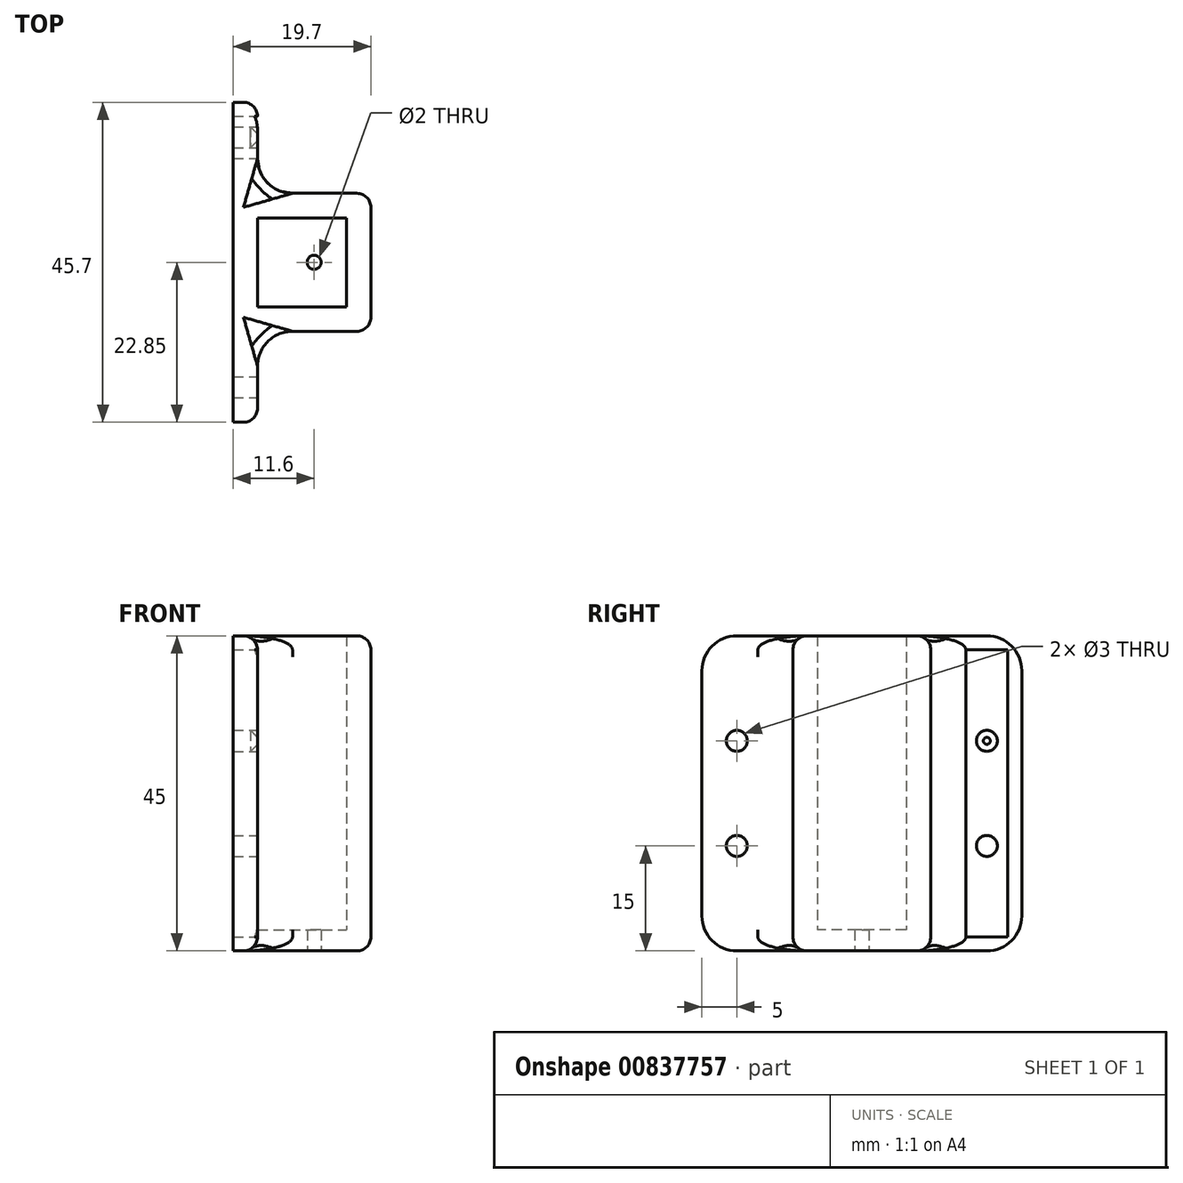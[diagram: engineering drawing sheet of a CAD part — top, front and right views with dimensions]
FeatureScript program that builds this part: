
annotation { "Feature Type Name" : "Feature", "Feature Type Description" : "" }
export const myFeature = defineFeature(function(context is Context, id is Id, definition is map)
    precondition{}
    {
        {
            var Q0;
            Q0=qCreatedBy(makeId("Top.planeOp"),FACE);
            var sketch = newSketch(context, id + "F0", { "sketchPlane" : qUnion([Q0])});
            skLineSegment(sketch, "E0.bottom", {"start": v(0, 6.35) * mm, "end": v(12.7, 6.35) * mm});
            skLineSegment(sketch, "E0.top", {"start": v(0, -6.35) * mm, "end": v(12.7, -6.35) * mm});
            skLineSegment(sketch, "E0.left", {"start": v(0, 6.35) * mm, "end": v(0, -6.35) * mm});
            skLineSegment(sketch, "E0.right", {"start": v(12.7, 6.35) * mm, "end": v(12.7, -6.35) * mm});
            skLineSegment(sketch, "E1.0", {"start": v(0, 9.85) * mm, "end": v(16.2, 9.85) * mm});
            skLineSegment(sketch, "E1.1", {"start": v(-3.5, 9.85) * mm, "end": v(-3.5, -9.85) * mm});
            skLineSegment(sketch, "E1.2", {"start": v(0, -9.85) * mm, "end": v(16.2, -9.85) * mm});
            skLineSegment(sketch, "E1.3", {"start": v(16.2, 9.85) * mm, "end": v(16.2, -9.85) * mm});
            skLineSegment(sketch, "E2.top", {"start": v(-3.5, 22.85) * mm, "end": v(0, 22.85) * mm});
            skLineSegment(sketch, "E2.left", {"start": v(-3.5, -9.85) * mm, "end": v(-3.5, 22.85) * mm});
            skLineSegment(sketch, "E3.trimOffspring", {"start": v(0, -6.35) * mm, "end": v(0, 6.35) * mm});
            skPoint(sketch, "E2.bottom.start.orphan", {"position": v(-3.5, -21.69) * mm});
            skLineSegment(sketch, "E4.trimOffspring", {"start": v(0, 9.85) * mm, "end": v(0, 22.85) * mm});
            skLineSegment(sketch, "E5.MirrorCS", {"start": v(0, -9.85) * mm, "end": v(0, -22.85) * mm});
            skLineSegment(sketch, "E6.MirrorCS", {"start": v(-3.5, -22.85) * mm, "end": v(0, -22.85) * mm});
            skLineSegment(sketch, "E7.MirrorCS", {"start": v(-3.5, 9.85) * mm, "end": v(-3.5, -22.85) * mm});
            skSolve(sketch);
        }
        {
            var Q0;
            Q0 = qSketchRegion(id + "F0", true);
            extrude(context, id + "F1", {"entities" : qUnion([Q0]), "depth" : 45 * mm, "offsetDistance" : 25 * mm});
        }
        {
            var Q0;
            Q0=makeQuery(id+"F0.imprint","IMPRINT",FACE,{"disambiguationData":[TD([[makeQuery(id+"F0.imprint","IMPRINT",EDGE,{"derivedFrom":sQuery(id+"F0.wireOp",EDGE,"E0.bottom")}),-1.0]])]});
            extrude(context, id + "F2", {"entities" : qUnion([Q0]), "operationType" : NewBodyOperationType.ADD, "depth" : 3 * mm, "offsetDistance" : 25 * mm});
        }
        {
            var Q0;
            {var subQ0=sQuery(id+"F0.wireOp",EDGE,"E3.trimOffspring");var subQ1=sQuery(id+"F0.wireOp",EDGE,"E0.right");var subQ2=sQuery(id+"F0.wireOp",EDGE,"E0.top");var subQ3=sQuery(id+"F0.wireOp",EDGE,"E0.bottom");Q0=makeQuery(id+"F2.boolean.opBoolean","MERGE",FACE,{"derivedFrom":[makeQuery(id+"F1.opExtrude","CAP_FACE",FACE,{"disambiguationData":[OSD([subQ3,subQ2,subQ1,sQuery(id+"F0.wireOp",EDGE,"E1.0"),sQuery(id+"F0.wireOp",EDGE,"E1.2"),sQuery(id+"F0.wireOp",EDGE,"E1.3"),sQuery(id+"F0.wireOp",EDGE,"E2.top"),sQuery(id+"F0.wireOp",EDGE,"E2.left"),subQ0,sQuery(id+"F0.wireOp",EDGE,"E4.trimOffspring"),sQuery(id+"F0.wireOp",EDGE,"E5.MirrorCS"),sQuery(id+"F0.wireOp",EDGE,"E6.MirrorCS"),sQuery(id+"F0.wireOp",EDGE,"E7.MirrorCS")])],"isStart":true}),makeQuery(id+"F2.opExtrude","CAP_FACE",FACE,{"disambiguationData":[OSD([subQ3,subQ2,subQ1,subQ0])],"isStart":true})]});}
            var sketch = newSketch(context, id + "F3", { "sketchPlane" : qUnion([Q0])});
            skLineSegment(sketch, "E8", {"start": v(0, 0) * mm, "end": v(16.2, 0) * mm, "construction": true});
            skCircle(sketch, "E9", {"center": v(8.1, 0) * mm, "radius": 1 * mm});
            skSolve(sketch);
        }
        {
            var Q0;
            Q0=makeQuery(id+"F3.imprint","IMPRINT",FACE,{"disambiguationData":[TD([[makeQuery(id+"F3.imprint","IMPRINT",EDGE,{"derivedFrom":sQuery(id+"F3.wireOp",EDGE,"E9")}),1.0]])]});
            extrude(context, id + "F4", {"entities" : qUnion([Q0]), "operationType" : NewBodyOperationType.REMOVE, "endBound" : BoundingType.THROUGH_ALL, "oppositeDirection" : true, "depth" : 25 * mm, "offsetDistance" : 25 * mm});
        }
        {
            var Q0;
            Q0=makeQuery(id+"F1.opExtrude","CAP_EDGE",EDGE,{"disambiguationData":[OSD([sQuery(id+"F0.wireOp",EDGE,"E6.MirrorCS")])],"isStart":false});
            var Q1;
            Q1=makeQuery(id+"F1.opExtrude","CAP_EDGE",EDGE,{"disambiguationData":[OSD([sQuery(id+"F0.wireOp",EDGE,"E2.top")])],"isStart":false});
            var Q2;
            Q2=makeQuery(id+"F1.opExtrude","CAP_EDGE",EDGE,{"disambiguationData":[OSD([sQuery(id+"F0.wireOp",EDGE,"E6.MirrorCS")])],"isStart":true});
            var Q3;
            Q3=makeQuery(id+"F1.opExtrude","CAP_EDGE",EDGE,{"disambiguationData":[OSD([sQuery(id+"F0.wireOp",EDGE,"E2.top")])],"isStart":true});
            fillet(context, id + "F5", {"entities" : qUnion([Q0, Q1, Q2, Q3]), "radius" : 5 * mm, "tangentPropagation" : true, "allowEdgeOverflow" : false});
        }
        {
            var Q0;
            Q0=makeQuery(id+"F1.opExtrude","CAP_EDGE",EDGE,{"disambiguationData":[OSD([sQuery(id+"F0.wireOp",EDGE,"E1.3")])],"isStart":false});
            var Q1;
            Q1=makeQuery(id+"F1.opExtrude","CAP_EDGE",EDGE,{"disambiguationData":[OSD([sQuery(id+"F0.wireOp",EDGE,"E1.2")])],"isStart":false});
            var Q2;
            Q2=makeQuery(id+"F1.opExtrude","CAP_EDGE",EDGE,{"disambiguationData":[OSD([sQuery(id+"F0.wireOp",EDGE,"E1.0")])],"isStart":false});
            var Q3;
            Q3=makeQuery(id+"F1.opExtrude","CAP_EDGE",EDGE,{"disambiguationData":[OSD([sQuery(id+"F0.wireOp",EDGE,"E4.trimOffspring")])],"isStart":false});
            var Q4;
            Q4=makeQuery(id+"F1.opExtrude","CAP_EDGE",EDGE,{"disambiguationData":[OSD([sQuery(id+"F0.wireOp",EDGE,"E5.MirrorCS")])],"isStart":false});
            var Q5;
            Q5=makeQuery(id+"F1.opExtrude","SWEPT_EDGE",EDGE,{"disambiguationData":[OSD([sQuery(id+"F0.wireOp",EDGE,"E5.MirrorCS"),sQuery(id+"F0.wireOp",EDGE,"E6.MirrorCS")])]});
            var Q6;
            Q6=makeQuery(id+"F1.opExtrude","SWEPT_EDGE",EDGE,{"disambiguationData":[OSD([sQuery(id+"F0.wireOp",EDGE,"E2.top"),sQuery(id+"F0.wireOp",EDGE,"E4.trimOffspring")])]});
            var Q7;
            Q7=makeQuery(id+"F1.opExtrude","SWEPT_EDGE",EDGE,{"disambiguationData":[OSD([sQuery(id+"F0.wireOp",EDGE,"E1.2"),sQuery(id+"F0.wireOp",EDGE,"E1.3")])]});
            var Q8;
            Q8=makeQuery(id+"F1.opExtrude","SWEPT_EDGE",EDGE,{"disambiguationData":[OSD([sQuery(id+"F0.wireOp",EDGE,"E1.0"),sQuery(id+"F0.wireOp",EDGE,"E1.3")])]});
            var Q9;
            Q9=makeQuery(id+"F1.opExtrude","CAP_EDGE",EDGE,{"disambiguationData":[OSD([sQuery(id+"F0.wireOp",EDGE,"E1.3")])],"isStart":true});
            var Q10;
            Q10=makeQuery(id+"F1.opExtrude","CAP_EDGE",EDGE,{"disambiguationData":[OSD([sQuery(id+"F0.wireOp",EDGE,"E1.2")])],"isStart":true});
            var Q11;
            Q11=makeQuery(id+"F1.opExtrude","CAP_EDGE",EDGE,{"disambiguationData":[OSD([sQuery(id+"F0.wireOp",EDGE,"E1.0")])],"isStart":true});
            var Q12;
            Q12=makeQuery(id+"F1.opExtrude","CAP_EDGE",EDGE,{"disambiguationData":[OSD([sQuery(id+"F0.wireOp",EDGE,"E5.MirrorCS")])],"isStart":true});
            var Q13;
            Q13=makeQuery(id+"F1.opExtrude","CAP_EDGE",EDGE,{"disambiguationData":[OSD([sQuery(id+"F0.wireOp",EDGE,"E4.trimOffspring")])],"isStart":true});
            fillet(context, id + "F6", {"entities" : qUnion([Q0, Q1, Q2, Q3, Q4, Q5, Q6, Q7, Q8, Q9, Q10, Q11, Q12, Q13]), "radius" : 2 * mm, "tangentPropagation" : true, "allowEdgeOverflow" : false});
        }
        {
            var Q0;
            Q0=makeQuery(id+"F1.opExtrude","SWEPT_EDGE",EDGE,{"disambiguationData":[OSD([sQuery(id+"F0.wireOp",EDGE,"E1.2"),sQuery(id+"F0.wireOp",EDGE,"E5.MirrorCS")])]});
            var Q1;
            Q1=makeQuery(id+"F1.opExtrude","SWEPT_EDGE",EDGE,{"disambiguationData":[OSD([sQuery(id+"F0.wireOp",EDGE,"E1.0"),sQuery(id+"F0.wireOp",EDGE,"E4.trimOffspring")])]});
            fillet(context, id + "F7", {"entities" : qUnion([Q0, Q1]), "radius" : 5 * mm, "tangentPropagation" : true, "allowEdgeOverflow" : false});
        }
        {
            var Q0;
            Q0=makeQuery(id+"F1.opExtrude","SWEPT_FACE",FACE,{"disambiguationData":[OSD([sQuery(id+"F0.wireOp",EDGE,"E5.MirrorCS")])]});
            var sketch = newSketch(context, id + "F8", { "sketchPlane" : qUnion([Q0])});
            skLineSegment(sketch, "E10.0.0", {"start": v(-20.85, 2) * mm, "end": v(-14.85, 2) * mm});
            skLineSegment(sketch, "E10.0.1", {"start": v(-14.85, 2) * mm, "end": v(-14.85, 43) * mm});
            skLineSegment(sketch, "E10.0.2", {"start": v(-14.85, 43) * mm, "end": v(-20.85, 43) * mm});
            skLineSegment(sketch, "E10.0.3", {"start": v(-20.85, 43) * mm, "end": v(-20.85, 2) * mm});
            skLineSegment(sketch, "E11.0.0", {"start": v(20.85, 43) * mm, "end": v(14.85, 43) * mm});
            skLineSegment(sketch, "E11.0.1", {"start": v(14.85, 43) * mm, "end": v(14.85, 2) * mm});
            skLineSegment(sketch, "E11.0.2", {"start": v(14.85, 2) * mm, "end": v(20.85, 2) * mm});
            skLineSegment(sketch, "E11.0.3", {"start": v(20.85, 2) * mm, "end": v(20.85, 43) * mm});
            skLineSegment(sketch, "E12", {"start": v(-17.85, 43) * mm, "end": v(-17.85, 2) * mm, "construction": true});
            skCircle(sketch, "E13", {"center": v(-17.85, 30) * mm, "radius": 1.5 * mm});
            skCircle(sketch, "E14", {"center": v(-17.85, 15) * mm, "radius": 1.5 * mm});
            skLineSegment(sketch, "E15", {"start": v(0, 0) * mm, "end": v(0, 47.04) * mm, "construction": true});
            skCircle(sketch, "E16.MirrorC", {"center": v(17.85, 30) * mm, "radius": 1.5 * mm});
            skCircle(sketch, "E17.MirrorC", {"center": v(17.85, 15) * mm, "radius": 1.5 * mm});
            skSolve(sketch);
        }
        {
            var Q0;
            Q0=makeQuery(id+"F8.imprint","IMPRINT",FACE,{"disambiguationData":[TD([[makeQuery(id+"F8.imprint","IMPRINT",EDGE,{"derivedFrom":sQuery(id+"F8.wireOp",EDGE,"E13")}),1.0]])]});
            var Q1;
            Q1=makeQuery(id+"F8.imprint","IMPRINT",FACE,{"disambiguationData":[TD([[makeQuery(id+"F8.imprint","IMPRINT",EDGE,{"derivedFrom":sQuery(id+"F8.wireOp",EDGE,"E14")}),1.0]])]});
            var Q2;
            Q2=makeQuery(id+"F8.imprint","IMPRINT",FACE,{"disambiguationData":[TD([[makeQuery(id+"F8.imprint","IMPRINT",EDGE,{"derivedFrom":sQuery(id+"F8.wireOp",EDGE,"E17.MirrorC")}),-1.0]])]});
            var Q3;
            Q3=makeQuery(id+"F8.imprint","IMPRINT",FACE,{"disambiguationData":[TD([[makeQuery(id+"F8.imprint","IMPRINT",EDGE,{"derivedFrom":sQuery(id+"F8.wireOp",EDGE,"E16.MirrorC")}),-1.0]])]});
            extrude(context, id + "F9", {"entities" : qUnion([Q0, Q1, Q2, Q3]), "operationType" : NewBodyOperationType.REMOVE, "endBound" : BoundingType.THROUGH_ALL, "oppositeDirection" : true, "depth" : 25 * mm, "offsetDistance" : 25 * mm});
        }
        {
            var Q0;
            Q0=makeQuery(id+"F9.boolean.opBoolean","COPY",EDGE,{"derivedFrom":makeQuery(id+"F9.opExtrude","CAP_EDGE",EDGE,{"disambiguationData":[OSD([sQuery(id+"F8.wireOp",EDGE,"E13")])],"isStart":true})});
            var Q1;
            Q1=makeQuery(id+"F9.boolean.opBoolean","COPY",EDGE,{"derivedFrom":makeQuery(id+"F9.opExtrude","CAP_EDGE",EDGE,{"disambiguationData":[OSD([sQuery(id+"F8.wireOp",EDGE,"E14")])],"isStart":true})});
            var Q2;
            Q2=makeQuery(id+"F9.boolean.opBoolean","COPY",EDGE,{"derivedFrom":makeQuery(id+"F9.opExtrude","CAP_EDGE",EDGE,{"disambiguationData":[OSD([sQuery(id+"F8.wireOp",EDGE,"E17.MirrorC")])],"isStart":true})});
            var Q3;
            Q3=makeQuery(id+"F9.boolean.opBoolean","COPY",EDGE,{"derivedFrom":makeQuery(id+"F9.opExtrude","CAP_EDGE",EDGE,{"disambiguationData":[OSD([sQuery(id+"F8.wireOp",EDGE,"E16.MirrorC")])],"isStart":true})});
            chamfer(context, id + "F10", {"entities" : qUnion([Q0, Q1, Q2, Q3]), "width" : 1 * mm, "tangentPropagation" : true});
        }
    });
